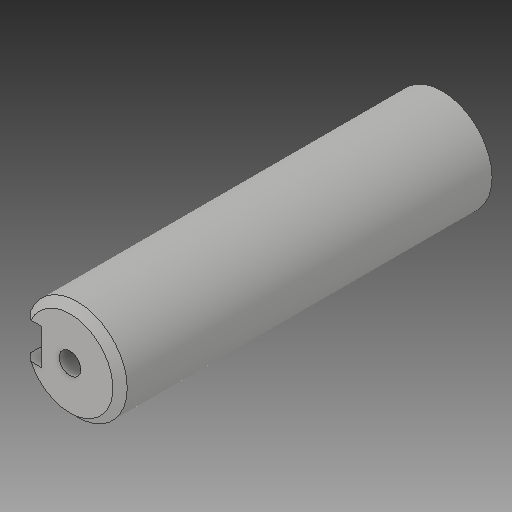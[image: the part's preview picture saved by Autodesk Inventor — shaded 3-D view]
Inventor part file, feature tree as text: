
AUTODESK INVENTOR PART (.ipt)
format: ipt  version: 2018 (Build 220112000, 112)  size: 119,296 bytes
history: native  units: mm
features: extrude x2, sketch x2, hole x1, plane x1, chamfer x1, projected_geometry x1
ambient origin geometry x8: Origin, YZ Plane, XZ Plane, XY Plane, X Axis, Y Axis, Z Axis, Center Point
bodies: Solid1 (feature_tree)
feature tree (8):
  extrude  "Extrusion1"  Depth=52.0mm TaperAngle=0.0deg
  hole  "Hole1"  [1 undecoded]
  plane  "Work Plane1"
  extrude  "Extrusion2"  TaperAngle=0.0deg  [1 undecoded]
  chamfer  "Chamfer1"  Distance=3.0mm
  sketch  "Sketch1"  dims[d0=14.0mm d1=52.0mm d2=0.0mm]
  sketch  "Sketch2"  dims[d3=10.0mm d4=10.0mm d5=3.0mm d6=6.0mm d7=4.0mm d8=2.0mm d9=90.0deg d10=13.0mm d11=0.0mm d12=5.0mm d14=0.0mm d17=3.0mm d18=0.0mm d19=1.0mm d20=2.0mm d21=45.0deg]
  projected_geometry  "Projected Loop1"
note: 2 required parameter values undecoded (feature->parameter linkage not recoverable at this tier; creation-order binding heuristic only, values carry confidence <= 0.55)
